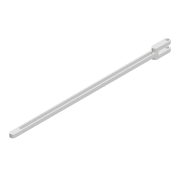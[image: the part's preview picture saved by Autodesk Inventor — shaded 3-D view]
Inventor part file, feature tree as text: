
AUTODESK INVENTOR PART (.ipt)
format: ipt  version: 2022 (Build 260153000, 153)  size: 154,624 bytes
history: native  units: mm
features: extrude x6, sketch x5, projected_geometry x4
ambient origin geometry x8: Origin, YZ Plane, XZ Plane, XY Plane, X Axis, Y Axis, Z Axis, Center Point
bodies: Solid1 (feature_tree)
feature tree (15):
  extrude  "Extrusion1"  Depth=6.0mm
  sketch  "Sketch2"  dims[d3=189.937mm d6=4.0mm d7=0.0mm]
  extrude  "Extrusion2"  Depth=4.0mm TaperAngle=0.0deg
  extrude  "Extrusion3"  Depth=3.2mm
  extrude  "Extrusion4"  Depth=10.0mm
  extrude  "Extrusion5"  Depth=4.0mm TaperAngle=0.0deg
  extrude  "Extrusion6"  Depth=6.0mm
  sketch  "Sketch1"  dims[d1=3.2mm d2=6.0mm]
  projected_geometry  "Projected Loop1"
  sketch  "Sketch3"  dims[d16=3.2mm d17=20.0mm]
  projected_geometry  "Projected Loop2"
  sketch  "Sketch4"  dims[d18=10.0mm d20=15.0mm]
  projected_geometry  "Projected Loop3"
  sketch  "Sketch5"  dims[d21=6.0mm d22=4.0mm d23=0.0mm d24=6.0mm d25=15.0mm d26=4.0mm d27=0.0mm d28=4.0mm d29=0.0mm d30=0.2mm d31=0.0mm d32=0.2mm d33=0.0mm]
  projected_geometry  "Projected Loop4"
